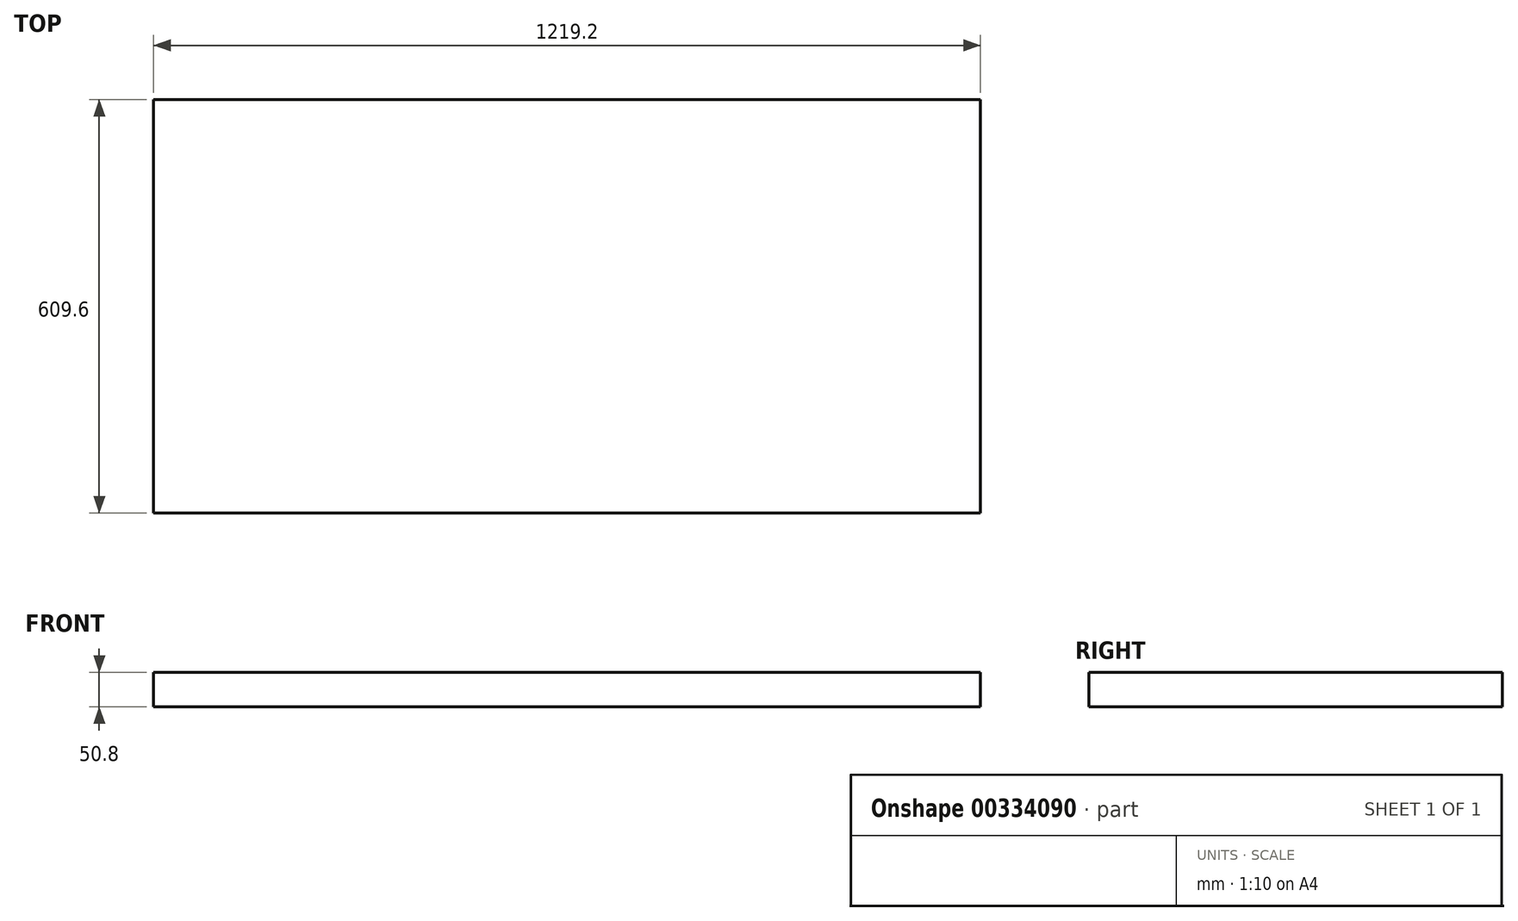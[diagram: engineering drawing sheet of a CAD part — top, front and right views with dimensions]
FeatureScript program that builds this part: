
annotation { "Feature Type Name" : "Feature", "Feature Type Description" : "" }
export const myFeature = defineFeature(function(context is Context, id is Id, definition is map)
    precondition{}
    {
        {
            var Q0;
            Q0=qCreatedBy(makeId("Front.planeOp"),FACE);
            var sketch = newSketch(context, id + "F0", { "sketchPlane" : qUnion([Q0])});
            skLineSegment(sketch, "E0.bottom", {"start": v(609.6, -25.4) * mm, "end": v(-609.6, -25.4) * mm});
            skLineSegment(sketch, "E0.top", {"start": v(609.6, 25.4) * mm, "end": v(-609.6, 25.4) * mm});
            skLineSegment(sketch, "E0.left", {"start": v(609.6, -25.4) * mm, "end": v(609.6, 25.4) * mm});
            skLineSegment(sketch, "E0.right", {"start": v(-609.6, -25.4) * mm, "end": v(-609.6, 25.4) * mm});
            skPoint(sketch, "E0.middle", {"position": v(0, 0) * mm});
            skSolve(sketch);
        }
        {
            var Q0;
            Q0 = qSketchRegion(id + "F0", true);
            extrude(context, id + "F1", {"entities" : qUnion([Q0]), "depth" : 609.6 * mm});
        }
    });
